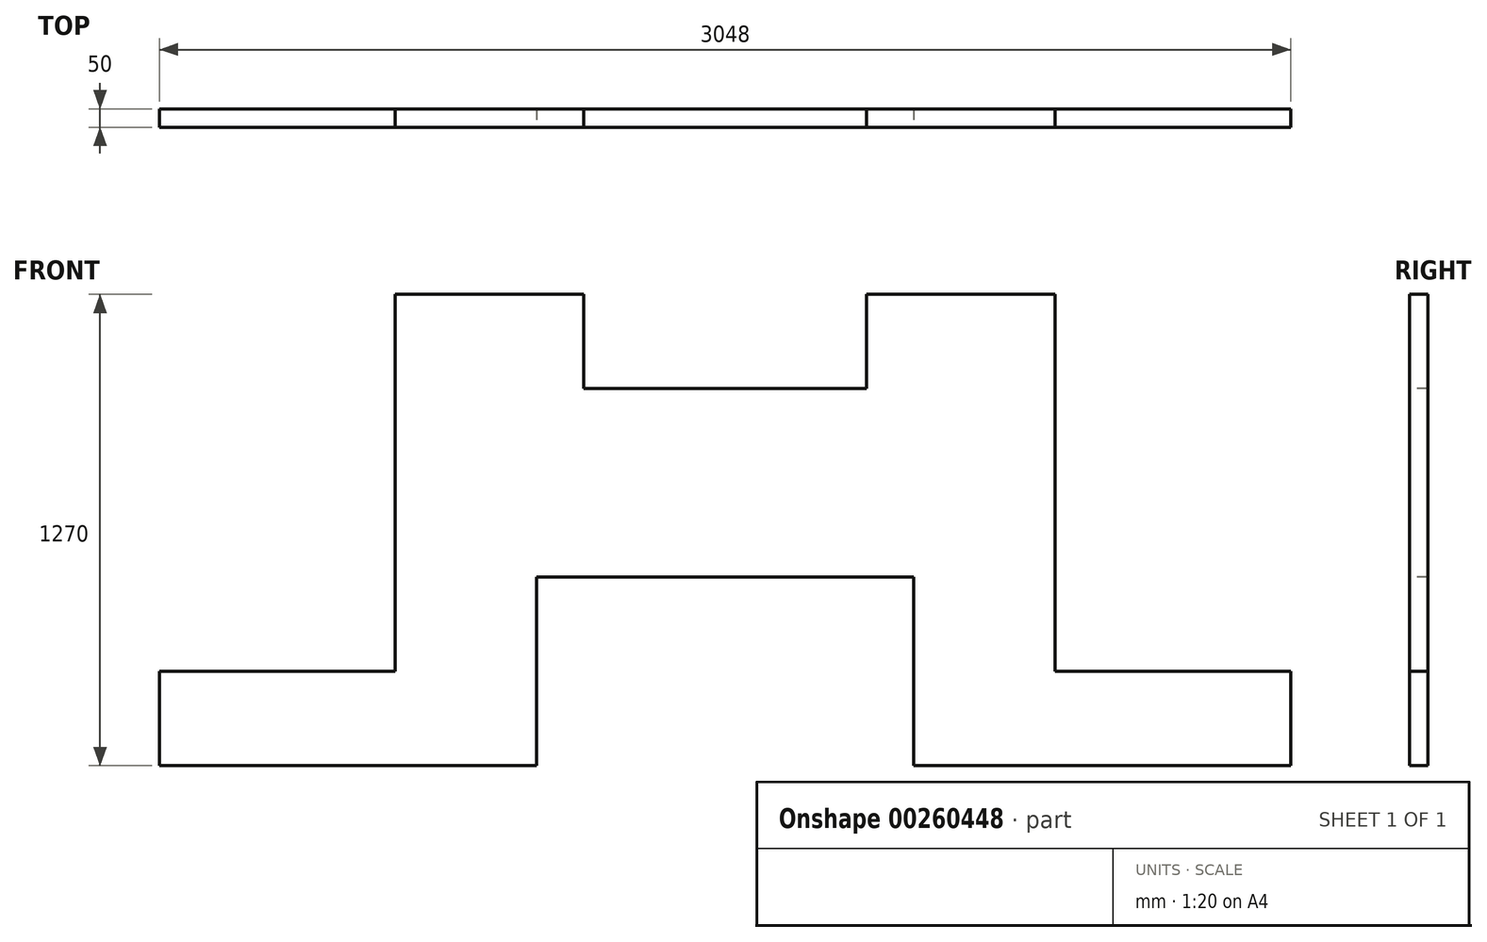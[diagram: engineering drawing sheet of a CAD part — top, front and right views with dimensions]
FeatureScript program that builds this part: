
annotation { "Feature Type Name" : "Feature", "Feature Type Description" : "" }
export const myFeature = defineFeature(function(context is Context, id is Id, definition is map)
    precondition{}
    {
        {
            assignVariable(context, id + "F0", {"name" : "A", "anyValue" : 50});
        }
        {
            var Q0;
            Q0=qCreatedBy(makeId("Front.planeOp"),FACE);
            var sketch = newSketch(context, id + "F1", { "sketchPlane" : qUnion([Q0])});
            skLineSegment(sketch, "E0", {"start": v(-1450.6, 0) * mm, "end": v(-1450.6, 254) * mm});
            skLineSegment(sketch, "E1", {"start": v(-1450.6, 254) * mm, "end": v(-815.6, 254) * mm});
            skLineSegment(sketch, "E2", {"start": v(-815.6, 254) * mm, "end": v(-815.6, 1270) * mm});
            skLineSegment(sketch, "E3", {"start": v(-815.6, 1270) * mm, "end": v(-307.6, 1270) * mm});
            skLineSegment(sketch, "E4", {"start": v(-307.6, 1270) * mm, "end": v(-307.6, 1016) * mm});
            skLineSegment(sketch, "E5", {"start": v(-307.6, 1016) * mm, "end": v(454.4, 1016) * mm});
            skLineSegment(sketch, "E6", {"start": v(454.4, 1016) * mm, "end": v(454.4, 1270) * mm});
            skLineSegment(sketch, "E7", {"start": v(454.4, 1270) * mm, "end": v(962.4, 1270) * mm});
            skLineSegment(sketch, "E8", {"start": v(962.4, 1270) * mm, "end": v(962.4, 254) * mm});
            skLineSegment(sketch, "E9", {"start": v(962.4, 254) * mm, "end": v(1597.4, 254) * mm});
            skLineSegment(sketch, "E10", {"start": v(1597.4, 254) * mm, "end": v(1597.4, 0) * mm});
            skLineSegment(sketch, "E11", {"start": v(1597.4, 0) * mm, "end": v(-1450.6, 0) * mm});
            skPoint(sketch, "E12.middle", {"position": v(0, 0) * mm});
            skLineSegment(sketch, "E13", {"start": v(-434.6, 0) * mm, "end": v(-434.6, 508) * mm});
            skLineSegment(sketch, "E14", {"start": v(-434.6, 508) * mm, "end": v(581.4, 508) * mm});
            skLineSegment(sketch, "E15", {"start": v(581.4, 508) * mm, "end": v(581.4, 0) * mm});
            skLineSegment(sketch, "E16", {"start": v(581.4, 0) * mm, "end": v(-434.6, 0) * mm});
            skSolve(sketch);
        }
        {
            var Q0;
            Q0 = qSketchRegion(id + "F1", true);
            extrude(context, id + "F2", {"entities" : qUnion([Q0]), "oppositeDirection" : true, "depth" : (getVariable(context, 'A')) * mm});
        }
        {
            var Q0;
            Q0=makeQuery(id+"F1.imprint","IMPRINT",FACE,{"disambiguationData":[TD([[makeQuery(id+"F1.imprint","IMPRINT",EDGE,{"derivedFrom":sQuery(id+"F1.wireOp",EDGE,"E13")}),-1.0]])]});
            extrude(context, id + "F3", {"entities" : qUnion([Q0]), "operationType" : NewBodyOperationType.REMOVE, "endBound" : BoundingType.THROUGH_ALL, "oppositeDirection" : true, "depth" : (getVariable(context, 'A')) * mm});
        }
        {
            var Q0;
            Q0=makeQuery(id+"F2.opExtrude","SWEPT_FACE",FACE,{"disambiguationData":[OSD([sQuery(id+"F1.wireOp",EDGE,"E3")])]});
            var sketch = newSketch(context, id + "F4", { "sketchPlane" : qUnion([Q0])});
            skLineSegment(sketch, "E17", {"start": v(-815.6, 1270) * mm, "end": v(-815.6, 1016) * mm});
            skLineSegment(sketch, "E18", {"start": v(-815.6, 1016) * mm, "end": v(-307.6, 1016) * mm});
            skLineSegment(sketch, "E19", {"start": v(-307.6, 1016) * mm, "end": v(-307.6, 1270) * mm});
            skLineSegment(sketch, "E20", {"start": v(-307.6, 1270) * mm, "end": v(-815.6, 1270) * mm});
            skLineSegment(sketch, "E21", {"start": v(-815.6, 254) * mm, "end": v(-815.6, 0) * mm});
            skLineSegment(sketch, "E22", {"start": v(-815.6, 0) * mm, "end": v(-307.6, 0) * mm});
            skLineSegment(sketch, "E23", {"start": v(-307.6, 0) * mm, "end": v(-307.6, 254) * mm});
            skLineSegment(sketch, "E24", {"start": v(-307.6, 254) * mm, "end": v(-815.6, 254) * mm});
            skLineSegment(sketch, "E25", {"start": v(-815.6, 1016) * mm, "end": v(-815.6, 254) * mm});
            skLineSegment(sketch, "E26", {"start": v(-307.6, 254) * mm, "end": v(-307.6, 1016) * mm});
            skSolve(sketch);
        }
        {
            var Q0;
            Q0=makeQuery(id+"F4.imprint","IMPRINT",FACE,{"disambiguationData":[TD([[makeQuery(id+"F4.imprint","IMPRINT",EDGE,{"derivedFrom":sQuery(id+"F4.wireOp",EDGE,"E18")}),-1.0]])]});
            extrude(context, id + "F5", {"entities" : qUnion([Q0]), "operationType" : NewBodyOperationType.REMOVE, "oppositeDirection" : true, "depth" : 508 * mm});
        }
        {
            var Q0;
            Q0=makeQuery(id+"F2.opExtrude","SWEPT_FACE",FACE,{"disambiguationData":[OSD([sQuery(id+"F1.wireOp",EDGE,"E7")])]});
            var sketch = newSketch(context, id + "F6", { "sketchPlane" : qUnion([Q0])});
            skLineSegment(sketch, "E27", {"start": v(962.4, 1016) * mm, "end": v(454.4, 1016) * mm});
            skLineSegment(sketch, "E28", {"start": v(454.4, 1016) * mm, "end": v(454.4, 254) * mm});
            skLineSegment(sketch, "E29", {"start": v(454.4, 254) * mm, "end": v(962.4, 254) * mm});
            skLineSegment(sketch, "E30", {"start": v(962.4, 254) * mm, "end": v(962.4, 1016) * mm});
            skSolve(sketch);
        }
        {
            var Q0;
            Q0=makeQuery(id+"F6.imprint","IMPRINT",FACE,{"disambiguationData":[TD([[makeQuery(id+"F6.imprint","IMPRINT",EDGE,{"derivedFrom":sQuery(id+"F6.wireOp",EDGE,"E27")}),1.0]])]});
            extrude(context, id + "F7", {"entities" : qUnion([Q0]), "operationType" : NewBodyOperationType.REMOVE, "oppositeDirection" : true, "depth" : 508 * mm});
        }
        {
            var Q0;
            Q0=makeQuery(id+"F2.opExtrude","SWEPT_FACE",FACE,{"disambiguationData":[OSD([sQuery(id+"F1.wireOp",EDGE,"E5")])]});
            var sketch = newSketch(context, id + "F8", { "sketchPlane" : qUnion([Q0])});
            skLineSegment(sketch, "E31", {"start": v(-307.6, 1016) * mm, "end": v(454.4, 1016) * mm});
            skLineSegment(sketch, "E32", {"start": v(454.4, 1016) * mm, "end": v(454.4, 254) * mm});
            skLineSegment(sketch, "E33", {"start": v(454.4, 254) * mm, "end": v(-307.6, 254) * mm});
            skLineSegment(sketch, "E34", {"start": v(-307.6, 254) * mm, "end": v(-307.6, 1016) * mm});
            skSolve(sketch);
        }
        {
            var Q0;
            Q0=makeQuery(id+"F8.imprint","IMPRINT",FACE,{"disambiguationData":[TD([[makeQuery(id+"F8.imprint","IMPRINT",EDGE,{"derivedFrom":sQuery(id+"F8.wireOp",EDGE,"E31")}),-1.0]])]});
            extrude(context, id + "F9", {"entities" : qUnion([Q0]), "operationType" : NewBodyOperationType.REMOVE, "oppositeDirection" : true, "depth" : 254 * mm});
        }
    });
